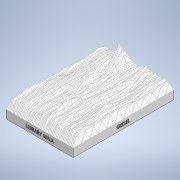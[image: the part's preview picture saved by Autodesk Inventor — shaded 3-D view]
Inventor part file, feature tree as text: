
AUTODESK INVENTOR PART (.ipt)
format: ipt  version: 2020 (Build 240168000, 168)  size: 2,445,312 bytes
history: native  units: in
note: dims shown in document units (in); Inventor stores cm internally (conversion verified against a paired STEP export)
features: extrude x6, sketch x6, projected_geometry x5, other x2
ambient origin geometry x8: Origin, YZ Plane, XZ Plane, XY Plane, X Axis, Y Axis, Z Axis, Center Point
bodies: Solid1 (feature_tree)
feature tree (19):
  other  "test"
  extrude  "Extrusion1"  Depth=8.0in
  extrude  "Extrusion2"  Depth=4.0in
  extrude  "Extrusion3"  Depth=2.0in
  extrude  "Extrusion4"  Depth=0.2in TaperAngle=0.0deg
  extrude  "Extrusion5"  Depth=1.0in
  extrude  "Extrusion6"  Depth=0.32in
  sketch  "Sketch1"  dims[d0=1.0in d1=0.0in d2=8.0in]
  sketch  "Sketch2"  dims[d3=1.0in d4=4.0in]
  projected_geometry  "Projected Loop1"
  sketch  "Sketch3"  dims[d5=0.32in d6=2.0in]
  projected_geometry  "Projected Loop2"
  sketch  "Sketch4"  dims[d7=0.34in d8=0.2in d9=0.0in]
  projected_geometry  "Projected Loop3"
  sketch  "Sketch5"  dims[d10=12.0in d11=1.0in]
  projected_geometry  "Projected Loop4"
  sketch  "Sketch6"  dims[d12=2.5in d13=0.32in d14=4.75in d15=0.34in d16=0.2in d17=0.0in d18=7.2in d19=8.0in d20=1.0in d21=0.4in d22=0.4in d23=0.3in d24=0.2in d25=0.0in d26=12.0in d27=1.0in d28=0.75in d29=0.125in d30=0.05in d31=0.975in d32=0.975in d33=0.5in d34=0.5in d35=0.25in d36=0.2375in d37=4.3307in d39=1.0in d40=0.3937in d42=1.0in d44=0.5in d45=0.5in d47=1.0in d48=0.25in d49=0.5in d50=0.5in d51=0.25in d52=1.0in d53=0.5in d54=0.5in d55=0.25in d56=1.0in d57=0.5in d58=0.5in d59=0.25in d60=1.0in d61=0.5in d62=0.5in d63=0.5in d64=0.5in d65=0.5in d66=0.5in d67=0.5in d68=0.5in d69=0.5in d70=0.5in d71=0.5in d72=0.5in d73=0.5in d74=0.5in d75=0.25in d76=1.0in d77=0.25in d78=1.0in d79=0.25in d80=1.0in d81=0.25in d82=1.0in d83=0.25in d84=1.0in d85=0.25in d86=1.0in d87=1.0in d88=0.25in d89=0.2in d90=0.0in d91=12.0in d92=8.0in d93=5.0in d94=4.0in d95=2.0in d96=3.5in d97=0.2in d98=0.0in]
  projected_geometry  "Projected Loop5"
  other  "MeshFeature1"
